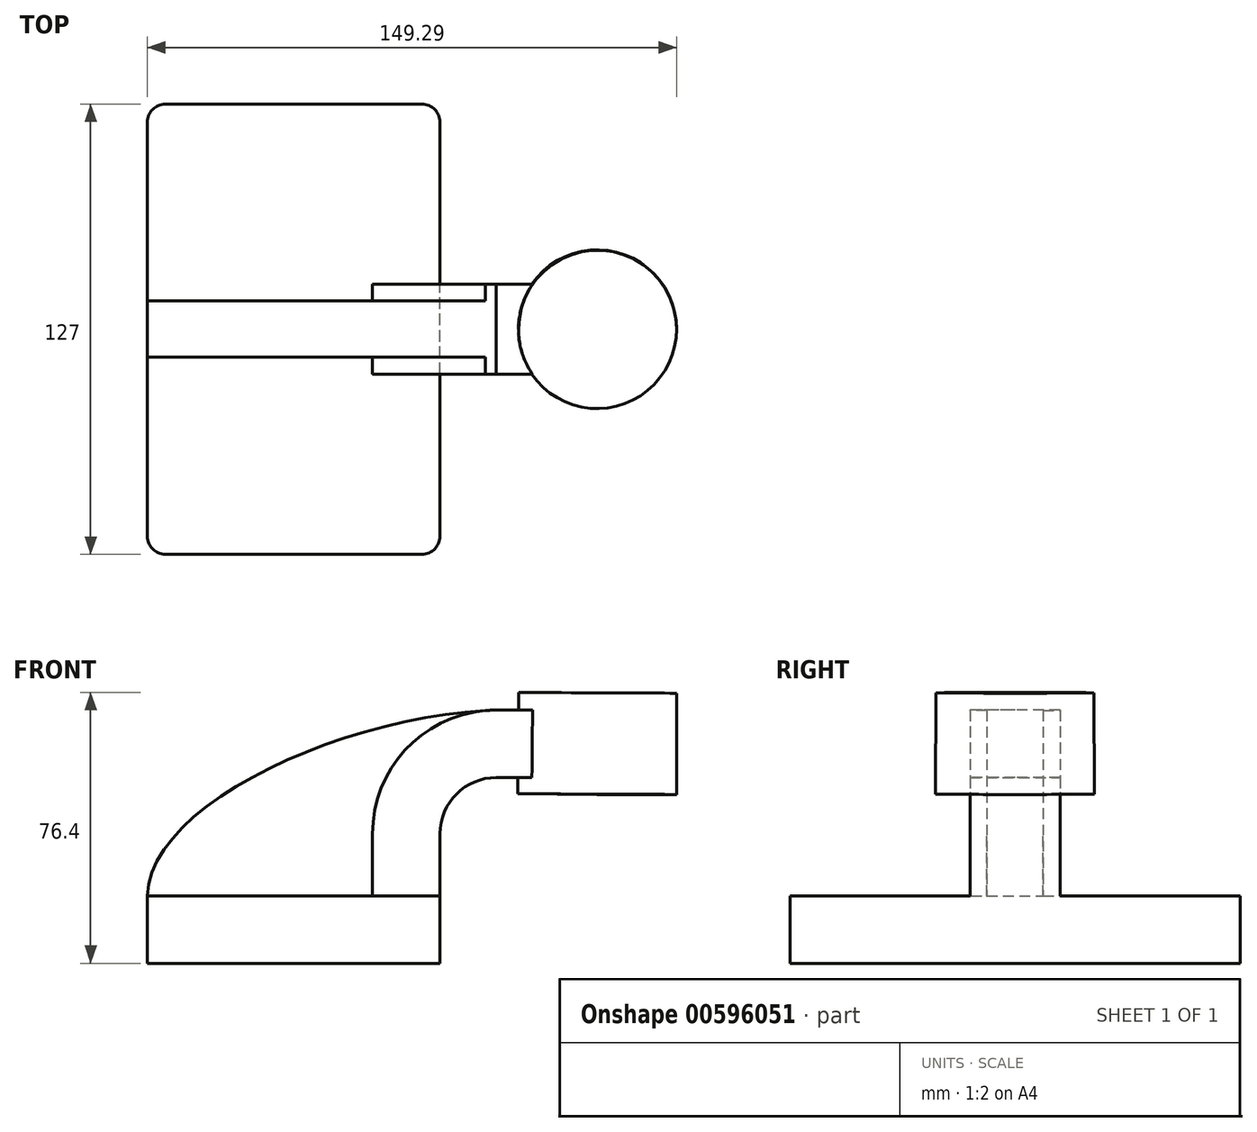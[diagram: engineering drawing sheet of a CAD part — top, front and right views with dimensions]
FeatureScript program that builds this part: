
annotation { "Feature Type Name" : "Feature", "Feature Type Description" : "" }
export const myFeature = defineFeature(function(context is Context, id is Id, definition is map)
    precondition{}
    {
        {
            var Q0;
            Q0=qCreatedBy(makeId("Front.planeOp"),FACE);
            var sketch = newSketch(context, id + "F0", { "sketchPlane" : qUnion([Q0])});
            skLineSegment(sketch, "E0.bottom", {"start": v(41.27, 9.53) * mm, "end": v(-41.28, 9.53) * mm});
            skLineSegment(sketch, "E0.top", {"start": v(41.28, -9.52) * mm, "end": v(-41.27, -9.52) * mm});
            skLineSegment(sketch, "E0.left", {"start": v(41.28, 9.53) * mm, "end": v(41.28, -9.52) * mm});
            skLineSegment(sketch, "E0.right", {"start": v(-41.28, 9.53) * mm, "end": v(-41.28, -9.52) * mm});
            skPoint(sketch, "E0.middle", {"position": v(0, 0) * mm});
            skLineSegment(sketch, "E1.bottom", {"start": v(57.2, 38.1) * mm, "end": v(108, 38.1) * mm});
            skLineSegment(sketch, "E1.top", {"start": v(57.2, 66.68) * mm, "end": v(108, 66.68) * mm});
            skLineSegment(sketch, "E1.left", {"start": v(57.2, 38.1) * mm, "end": v(57.2, 66.68) * mm});
            skLineSegment(sketch, "E1.right", {"start": v(108, 38.1) * mm, "end": v(108, 66.68) * mm});
            skPoint(sketch, "E1.middle", {"position": v(82.6, 52.39) * mm});
            skLineSegment(sketch, "E2", {"start": v(41.27, 9.53) * mm, "end": v(41.27, 27) * mm});
            skArc(sketch, "E3", {"start": v(41.27, 27) * mm, "mid": v(45.92, 38.23) * mm, "end": v(57.15, 42.88) * mm});
            skLineSegment(sketch, "E4", {"start": v(57.15, 42.88) * mm, "end": v(85.72, 42.88) * mm});
            skLineSegment(sketch, "E5.0", {"start": v(57.15, 61.93) * mm, "end": v(85.72, 61.93) * mm});
            skArc(sketch, "E5.1", {"start": v(22.22, 27) * mm, "mid": v(32.45, 51.7) * mm, "end": v(57.15, 61.93) * mm});
            skLineSegment(sketch, "E5.2", {"start": v(22.22, 9.53) * mm, "end": v(22.22, 27) * mm});
            skLineSegment(sketch, "E6", {"start": v(85.6, 38.1) * mm, "end": v(85.72, 66.68) * mm});
            skFitSpline(sketch, "E7", {"points": [v(57.15, 61.93) * mm, v(-41.28, 9.52) * mm], "startDerivative": vector(-128.82, -4.08) * mm, "endDerivative": vector(-1.3, -77.47) * mm});
            skSolve(sketch);
        }
        {
            var Q0;
            Q0=makeQuery(id+"F0.imprint","IMPRINT",FACE,{"disambiguationData":[TD([[makeQuery(id+"F0.imprint","IMPRINT",EDGE,{"derivedFrom":sQuery(id+"F0.wireOp",EDGE,"E0.top")}),-1.0]])]});
            extrude(context, id + "F1", {"entities" : qUnion([Q0]), "endBound" : BoundingType.SYMMETRIC, "depth" : 127 * mm, "offsetDistance" : 25.4 * mm});
        }
        {
            var Q0;
            {var subQ6=sQuery(id+"F0.wireOp",EDGE,"E2");Q0=makeQuery(id+"F0.imprint","IMPRINT",FACE,{"disambiguationData":[TD([[makeQuery(id+"F0.imprint","IMPRINT",EDGE,{"derivedFrom":subQ6}),1.0]])]});}
            var Q1;
            {var subQ0=sQuery(id+"F0.wireOp",EDGE,"E4");var subQ1=sQuery(id+"F0.wireOp",EDGE,"E1.left");var subQ2=makeQuery(id+"F0.imprint","INTERSECT",VERTEX,{"derivedFrom":[subQ1,subQ0]});Q1=makeQuery(id+"F0.imprint","IMPRINT",FACE,{"disambiguationData":[TD([[makeQuery(id+"F0.imprint","IMPRINT",EDGE,{"disambiguationData":[TD([[subQ2,-1.0]])],"derivedFrom":subQ1}),-1.0]])]});}
            extrude(context, id + "F2", {"entities" : qUnion([Q0, Q1]), "operationType" : NewBodyOperationType.ADD, "endBound" : BoundingType.SYMMETRIC, "depth" : 25.4 * mm, "offsetDistance" : 25.4 * mm});
        }
        {
            var Q0;
            {var subQ3=sQuery(id+"F0.wireOp",EDGE,"E5.2");Q0=makeQuery(id+"F0.imprint","IMPRINT",FACE,{"disambiguationData":[TD([[makeQuery(id+"F0.imprint","IMPRINT",EDGE,{"derivedFrom":subQ3}),1.0]])]});}
            extrude(context, id + "F3", {"entities" : qUnion([Q0]), "operationType" : NewBodyOperationType.ADD, "endBound" : BoundingType.SYMMETRIC, "depth" : 15.88 * mm, "offsetDistance" : 25.4 * mm});
        }
        {
            var Q0;
            {var subQ4=sQuery(id+"F0.wireOp",EDGE,"E1.right");Q0=makeQuery(id+"F0.imprint","IMPRINT",FACE,{"disambiguationData":[TD([[makeQuery(id+"F0.imprint","IMPRINT",EDGE,{"derivedFrom":subQ4}),1.0]])]});}
            var Q1;
            Q1=sQuery(id+"F0.wireOp",EDGE,"E6");
            revolve(context, id + "F4", {"operationType" : NewBodyOperationType.ADD, "entities" : qUnion([Q0]), "axis" : qUnion([Q1]), "revolveType" : RevolveType.FULL});
        }
        {
            var Q0;
            Q0=makeQuery(id+"F1.opExtrude","CAP_EDGE",EDGE,{"disambiguationData":[OSD([sQuery(id+"F0.wireOp",EDGE,"E0.right")])],"isStart":true});
            var Q1;
            Q1=makeQuery(id+"F1.opExtrude","CAP_EDGE",EDGE,{"disambiguationData":[OSD([sQuery(id+"F0.wireOp",EDGE,"E0.right")])],"isStart":false});
            var Q2;
            Q2=makeQuery(id+"F1.opExtrude","CAP_EDGE",EDGE,{"disambiguationData":[OSD([sQuery(id+"F0.wireOp",EDGE,"E0.left")])],"isStart":false});
            var Q3;
            Q3=makeQuery(id+"F1.opExtrude","CAP_EDGE",EDGE,{"disambiguationData":[OSD([sQuery(id+"F0.wireOp",EDGE,"E0.left")])],"isStart":true});
            fillet(context, id + "F5", {"entities" : qUnion([Q0, Q1, Q2, Q3]), "radius" : 5.08 * mm, "tangentPropagation" : true, "allowEdgeOverflow" : false});
        }
    });
